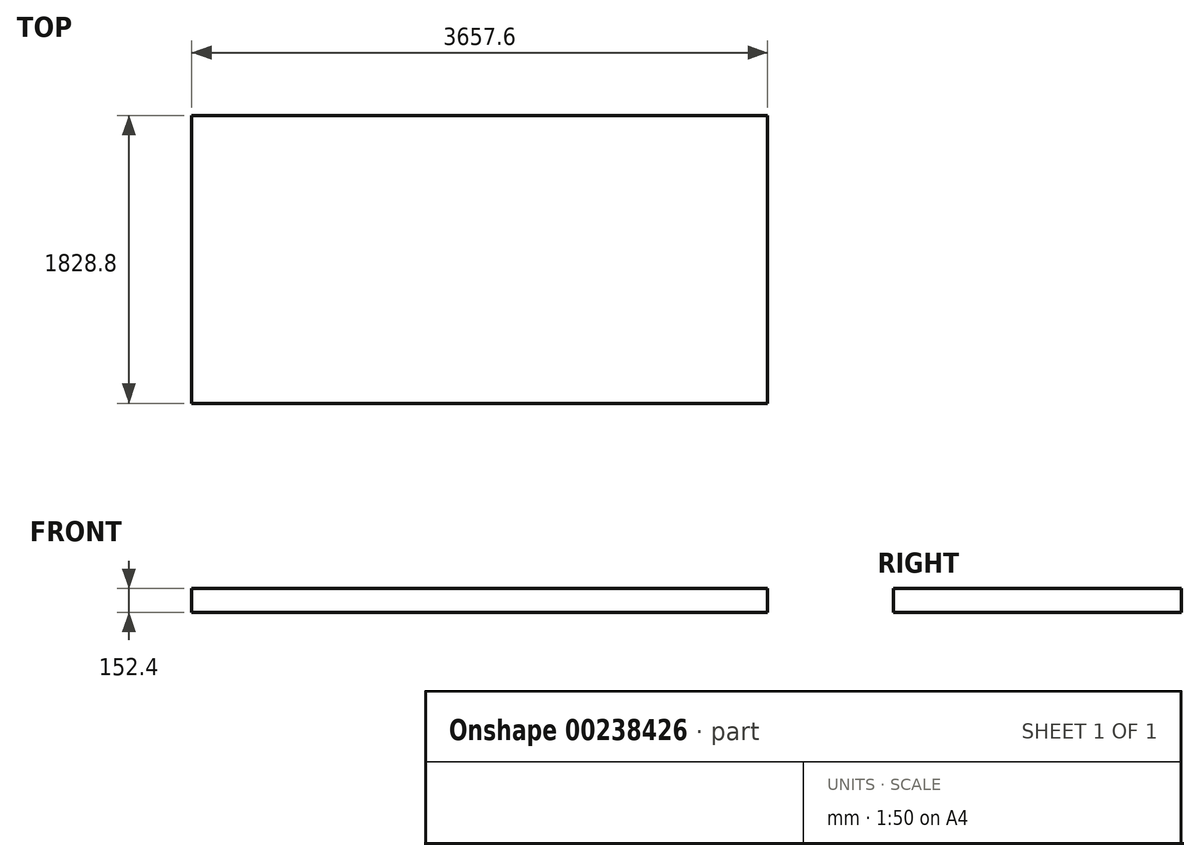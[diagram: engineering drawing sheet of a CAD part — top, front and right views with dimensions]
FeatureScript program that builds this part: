
annotation { "Feature Type Name" : "Feature", "Feature Type Description" : "" }
export const myFeature = defineFeature(function(context is Context, id is Id, definition is map)
    precondition{}
    {
        {
            var Q0;
            Q0=qCreatedBy(makeId("Top.planeOp"),FACE);
            var sketch = newSketch(context, id + "F0", { "sketchPlane" : qUnion([Q0])});
            skLineSegment(sketch, "E0.bottom", {"start": v(-36.8, 1816.12) * mm, "end": v(3620.8, 1816.12) * mm});
            skLineSegment(sketch, "E0.top", {"start": v(-36.8, -12.68) * mm, "end": v(3620.8, -12.68) * mm});
            skLineSegment(sketch, "E0.left", {"start": v(-36.8, 1816.12) * mm, "end": v(-36.8, -12.68) * mm});
            skLineSegment(sketch, "E0.right", {"start": v(3620.8, 1816.12) * mm, "end": v(3620.8, -12.68) * mm});
            skSolve(sketch);
        }
        {
            var Q0;
            Q0=makeQuery(id+"F0.imprint","IMPRINT",FACE,{"disambiguationData":[TD([[makeQuery(id+"F0.imprint","IMPRINT",EDGE,{"derivedFrom":sQuery(id+"F0.wireOp",EDGE,"E0.bottom")}),-1.0]])]});
            extrude(context, id + "F1", {"entities" : qUnion([Q0]), "depth" : 152.4 * mm});
        }
    });
